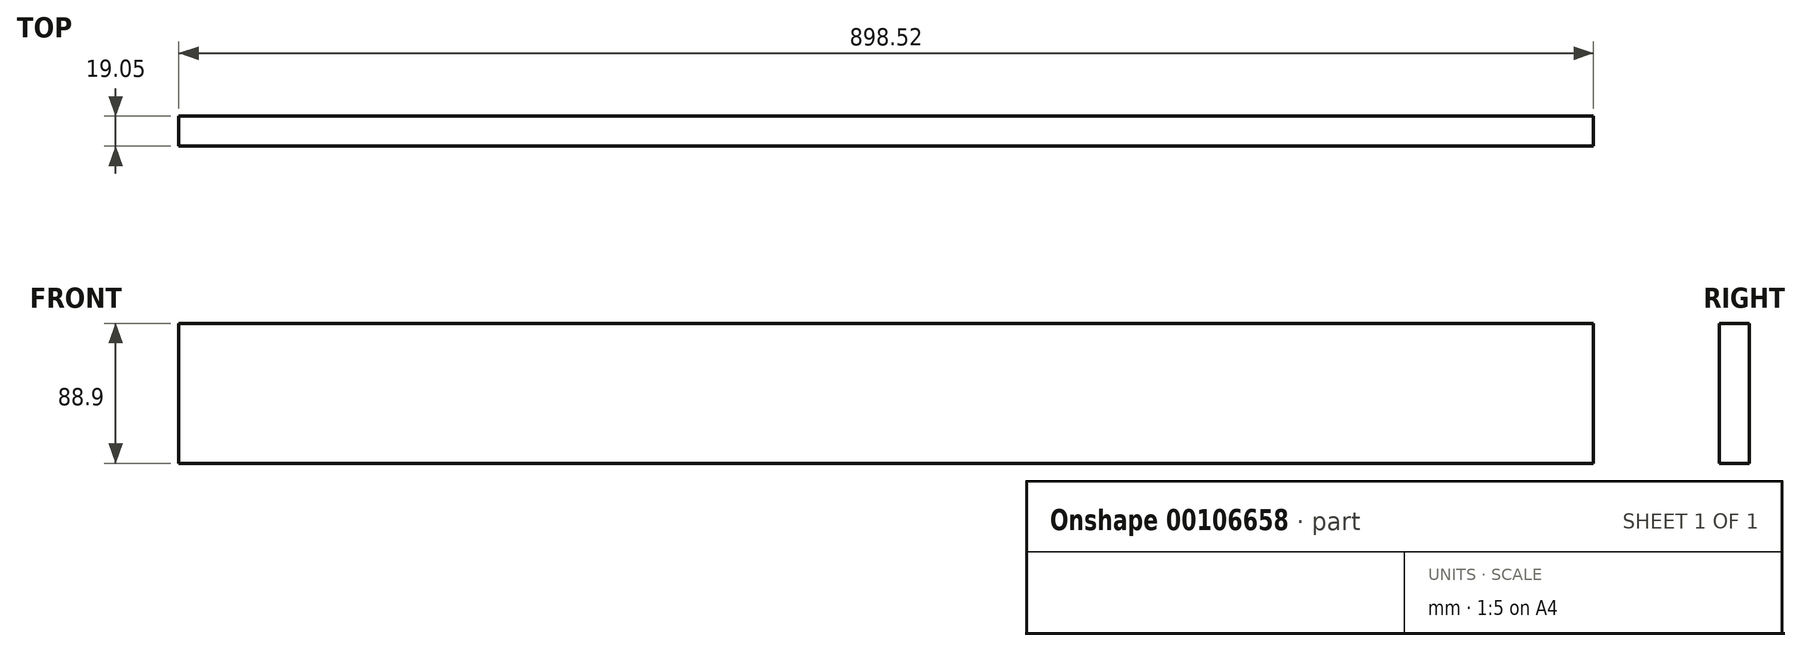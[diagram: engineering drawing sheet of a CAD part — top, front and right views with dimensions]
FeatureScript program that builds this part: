
annotation { "Feature Type Name" : "Feature", "Feature Type Description" : "" }
export const myFeature = defineFeature(function(context is Context, id is Id, definition is map)
    precondition{}
    {
        {
            var Q0;
            Q0=qCreatedBy(makeId("Front.planeOp"),FACE);
            var sketch = newSketch(context, id + "F0", { "sketchPlane" : qUnion([Q0])});
            skLineSegment(sketch, "E0.bottom", {"start": v(0, 0) * mm, "end": v(898.52, 0) * mm});
            skLineSegment(sketch, "E0.top", {"start": v(0, 88.9) * mm, "end": v(898.52, 88.9) * mm});
            skLineSegment(sketch, "E0.left", {"start": v(0, 0) * mm, "end": v(0, 88.9) * mm});
            skLineSegment(sketch, "E0.right", {"start": v(898.52, 0) * mm, "end": v(898.52, 88.9) * mm});
            skSolve(sketch);
        }
        {
            var Q0;
            Q0=makeQuery(id+"F0.imprint","IMPRINT",FACE,{"disambiguationData":[TD([[makeQuery(id+"F0.imprint","IMPRINT",EDGE,{"derivedFrom":sQuery(id+"F0.wireOp",EDGE,"E0.bottom")}),1.0]])]});
            extrude(context, id + "F1", {"entities" : qUnion([Q0]), "depth" : 19.05 * mm});
        }
    });
